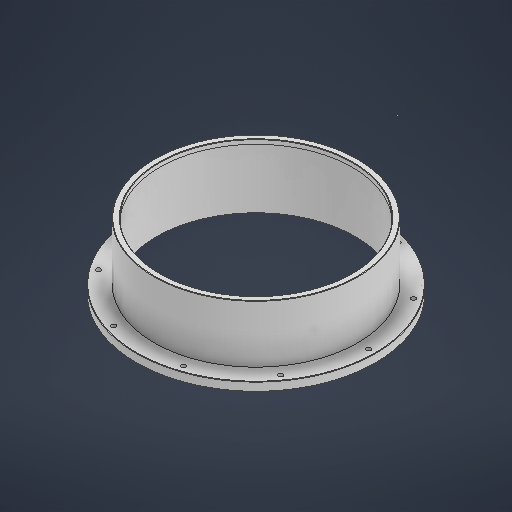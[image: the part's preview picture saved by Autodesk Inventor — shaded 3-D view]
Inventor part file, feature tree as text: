
AUTODESK INVENTOR PART (.ipt)
format: ipt  version: 2025 (Build 290162000, 162)  size: 299,520 bytes
history: native  units: in
note: dims shown in document units (in); Inventor stores cm internally (conversion verified against a paired STEP export)
features: other x12, sketch x6, extrude x4, chamfer x2, hole x1
ambient origin geometry x8: Origin, YZ Plane, XZ Plane, XY Plane, X Axis, Y Axis, Z Axis, Center Point
bodies: Solid1 (feature_tree)
feature tree (25):
  other  "Table"
  other  "Cylinder Segment - 01"
  other  "Cylinder Segment - 02"
  other  "Cylinder Segment - 03"
  other  "Cylinder Segment - 04"
  other  "Cylinder Segment - 05"
  other  "Cylinder Segment - 06"
  other  "Cylinder Segment - 07"
  other  "Cylinder Segment - 08"
  other  "Cylinder Segment - 09"
  other  "Cylinder Segment - 10"
  other  "Cylinder Segment - Face"
  sketch  "Sketch1"  dims[d5=0.0in d7=0.0in]
  extrude  "Extrusion1"  TaperAngle=0.0deg  [1 undecoded]
  extrude  "Extrusion2"  Depth=0.0787in TaperAngle=45.0deg
  extrude  "Extrusion7"  Depth=10.0394in
  chamfer  "Chamfer1"  Distance=3.937in Angle=360.0deg
  chamfer  "Chamfer2"  Distance=0.3937in
  extrude  "Extrusion8"  Depth=0.0787in
  hole  "Hole1"  [1 undecoded]
  sketch  "Sketch2"  dims[d25=0.0787in d26=45.0deg d27=10.0394in]
  sketch  "Sketch3"  dims[d35=3.1496in d36=0.0787in]
  sketch  "Sketch Circular Pattern1"  dims[d18=0.0in d22=0.0787in d23=45.0deg]
  sketch  "Sketch4"  dims[d37=2.7559in d39=360.0deg d41=0.0617in d42=0.1575in d43=0.1575in d44=0.0787in d45=90.0deg d46=0.248in d47=0.8108in]
  sketch  "Sketch Circular Pattern2"  dims[d28=0.1969in d29=3.937in d31=360.0deg d33=0.3937in d34=0.0in]
note: 2 required parameter values undecoded (feature->parameter linkage not recoverable at this tier; creation-order binding heuristic only, values carry confidence <= 0.55)
